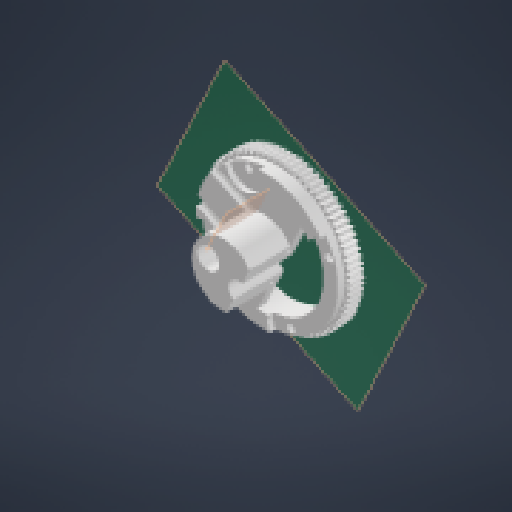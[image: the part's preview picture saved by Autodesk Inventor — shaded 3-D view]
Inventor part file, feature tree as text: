
AUTODESK INVENTOR PART (.ipt)
format: ipt  version: 2023.2 (Build 272271000, 271)  size: 925,696 bytes
history: native  units: in
note: dims shown in document units (in); Inventor stores cm internally (conversion verified against a paired STEP export)
features: reference x8, extrude x7, plane x5, sketch x5, other x4, thicken_offset x1, imported_body x1
ambient origin geometry x8: Origin, YZ Plane, XZ Plane, XY Plane, X Axis, Y Axis, Z Axis, Center Point
bodies: Solid1 (feature_tree), Solid2 (feature_tree)
feature tree (31):
  plane  "Work Plane1"
  plane  "Work Plane2"
  extrude  "Extrusion1"  Depth=0.3937in TaperAngle=0.0deg
  sketch  "Sketch2"  dims[d0=0.1181in d1=0.3937in d2=0.0in]
  plane  "Work Plane3"
  plane  "Work Plane4"
  extrude  "Extrusion3"  Depth=0.3937in TaperAngle=0.0deg
  extrude  "Extrusion4"  Depth=0.1969in
  thicken_offset  "Thicken1"
  extrude  "Extrusion5"  Depth=0.7874in
  extrude  "Extrusion6"  Depth=0.7874in
  plane  "Work Plane5"
  extrude  "Extrusion7"  Depth=0.1181in TaperAngle=0.0deg
  extrude  "Extrusion8"  TaperAngle=0.0deg  [1 undecoded]
  imported_body  "Base1"
  reference  "Reference2"
  reference  "Reference3"
  reference  "Reference4"
  sketch  "Sketch3"  dims[d5=0.3937in d6=0.0in d7=0.1969in d8=0.0in]
  reference  "Reference5"
  reference  "Reference6"
  sketch  "Sketch5"  dims[d9=0.1969in d10=0.1969in]
  reference  "Reference7"
  reference  "Reference8"
  sketch  "Sketch6"  dims[d11=0.7874in d12=0.7874in]
  sketch  "Sketch7"  dims[d13=0.7874in d14=0.7874in d15=0.1181in d16=0.0in d17=0.0in d18=0.0in d19=-0.7874in d20=0.2165in d21=0.2165in d22=0.0in d23=0.0in d24=2.9921in d25=0.0in d26=0.0in]
  reference  "Reference9"
  parser-record x1  (decoder bookkeeping rows leaked as tree rows — omitted from the tree; the rows remain in map.json)
  other  "turret_assembly.iam"
  other  "small_actuator_holder:1"
  other  "horizontal_axis_hal_gear:1"
note: 1 required parameter value undecoded (feature->parameter linkage not recoverable at this tier; creation-order binding heuristic only, values carry confidence <= 0.55)
note: 1 file-system path scrubbed to <path> (originals preserved in map.json)
